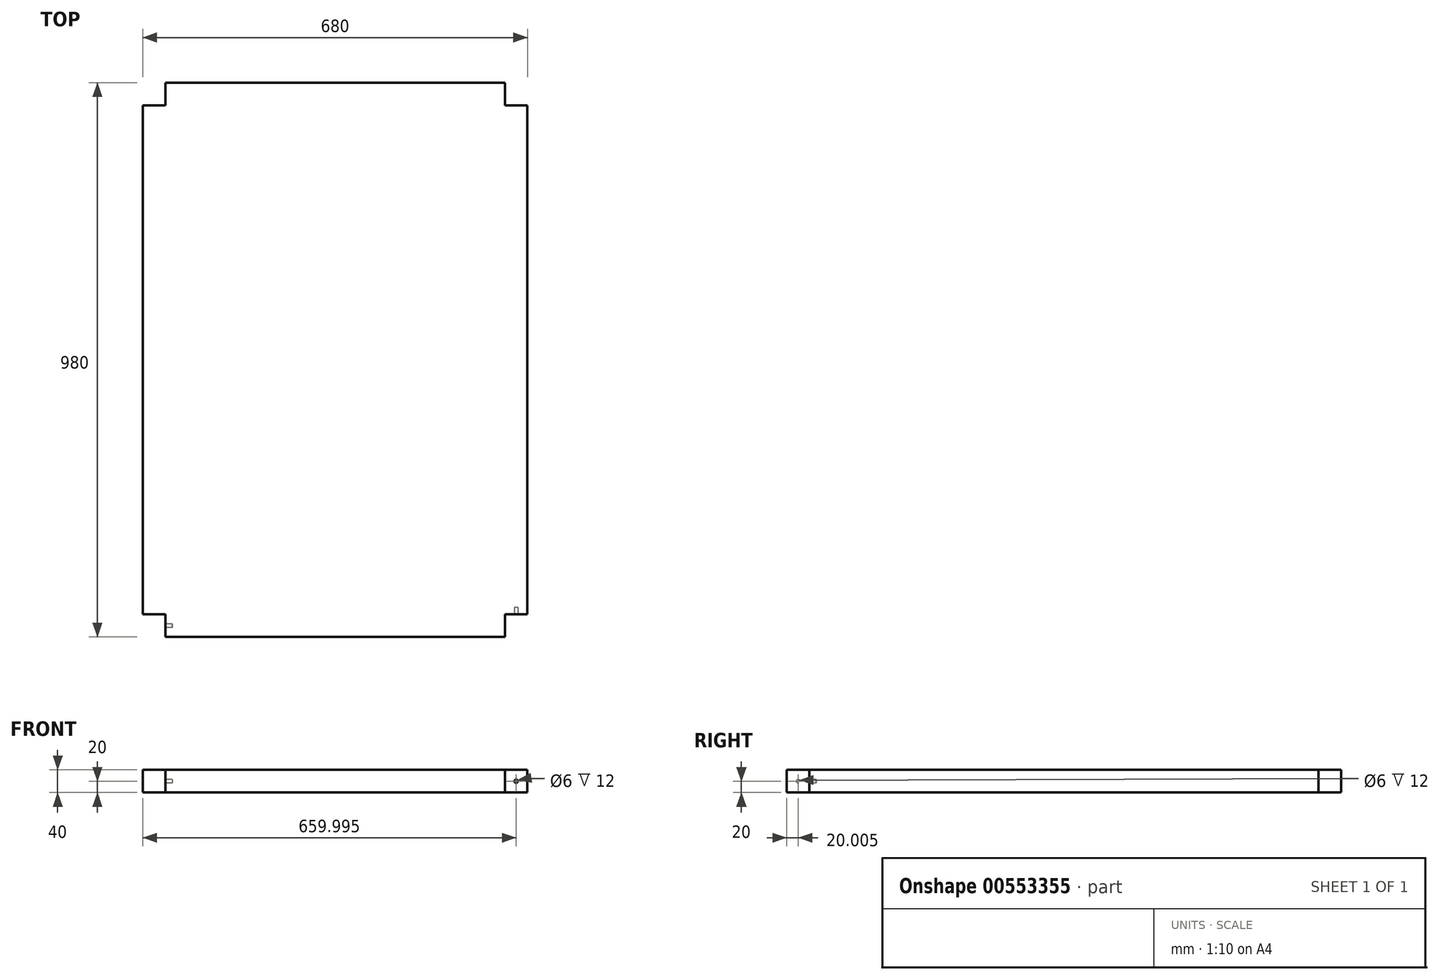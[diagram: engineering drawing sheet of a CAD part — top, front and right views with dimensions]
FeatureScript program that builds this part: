
annotation { "Feature Type Name" : "Feature", "Feature Type Description" : "" }
export const myFeature = defineFeature(function(context is Context, id is Id, definition is map)
    precondition{}
    {
        {
            var Q0;
            Q0=qCreatedBy(makeId("Top.planeOp"),FACE);
            var sketch = newSketch(context, id + "F0", { "sketchPlane" : qUnion([Q0])});
            skLineSegment(sketch, "E0.bottom", {"start": v(-662.47, 921.5) * mm, "end": v(17.53, 921.5) * mm});
            skLineSegment(sketch, "E0.top", {"start": v(-662.47, -58.5) * mm, "end": v(17.53, -58.5) * mm});
            skLineSegment(sketch, "E0.left", {"start": v(-662.47, 921.5) * mm, "end": v(-662.47, -58.5) * mm});
            skLineSegment(sketch, "E0.right", {"start": v(17.53, 921.5) * mm, "end": v(17.53, -58.5) * mm});
            skSolve(sketch);
        }
        {
            var Q0;
            Q0=makeQuery(id+"F0.imprint","IMPRINT",FACE,{"disambiguationData":[TD([[makeQuery(id+"F0.imprint","IMPRINT",EDGE,{"derivedFrom":sQuery(id+"F0.wireOp",EDGE,"E0.bottom")}),-1.0]])]});
            extrude(context, id + "F1", {"entities" : qUnion([Q0]), "depth" : 40 * mm, "offsetDistance" : 25 * mm});
        }
        {
            var Q0;
            Q0=makeQuery(id+"F1.opExtrude","CAP_FACE",FACE,{"disambiguationData":[OSD([sQuery(id+"F0.wireOp",EDGE,"E0.bottom"),sQuery(id+"F0.wireOp",EDGE,"E0.top"),sQuery(id+"F0.wireOp",EDGE,"E0.left"),sQuery(id+"F0.wireOp",EDGE,"E0.right")])],"isStart":false});
            var sketch = newSketch(context, id + "F2", { "sketchPlane" : qUnion([Q0])});
            skLineSegment(sketch, "E1.bottom", {"start": v(-662.47, 921.5) * mm, "end": v(-622.47, 921.5) * mm});
            skLineSegment(sketch, "E1.top", {"start": v(-662.47, 881.5) * mm, "end": v(-622.47, 881.5) * mm});
            skLineSegment(sketch, "E1.left", {"start": v(-662.47, 921.5) * mm, "end": v(-662.47, 881.5) * mm});
            skLineSegment(sketch, "E1.right", {"start": v(-622.47, 921.5) * mm, "end": v(-622.47, 881.5) * mm});
            skLineSegment(sketch, "E2.bottom", {"start": v(17.53, 921.5) * mm, "end": v(-22.47, 921.5) * mm});
            skLineSegment(sketch, "E2.top", {"start": v(17.53, 881.5) * mm, "end": v(-22.47, 881.5) * mm});
            skLineSegment(sketch, "E2.left", {"start": v(17.53, 921.5) * mm, "end": v(17.53, 881.5) * mm});
            skLineSegment(sketch, "E2.right", {"start": v(-22.47, 921.5) * mm, "end": v(-22.47, 881.5) * mm});
            skLineSegment(sketch, "E3.bottom", {"start": v(-662.47, -58.5) * mm, "end": v(-622.47, -58.5) * mm});
            skLineSegment(sketch, "E3.top", {"start": v(-662.47, -18.5) * mm, "end": v(-622.47, -18.5) * mm});
            skLineSegment(sketch, "E3.left", {"start": v(-662.47, -58.5) * mm, "end": v(-662.47, -18.5) * mm});
            skLineSegment(sketch, "E3.right", {"start": v(-622.47, -58.5) * mm, "end": v(-622.47, -18.5) * mm});
            skLineSegment(sketch, "E4.bottom", {"start": v(17.53, -58.5) * mm, "end": v(-22.47, -58.5) * mm});
            skLineSegment(sketch, "E4.top", {"start": v(17.53, -18.5) * mm, "end": v(-22.47, -18.5) * mm});
            skLineSegment(sketch, "E4.left", {"start": v(17.53, -58.5) * mm, "end": v(17.53, -18.5) * mm});
            skLineSegment(sketch, "E4.right", {"start": v(-22.47, -58.5) * mm, "end": v(-22.47, -18.5) * mm});
            skSolve(sketch);
        }
        {
            var Q0;
            Q0=qSketchRegion(id+"F2",true);
            extrude(context, id + "F3", {"entities" : qUnion([Q0]), "operationType" : NewBodyOperationType.REMOVE, "oppositeDirection" : true, "depth" : 40 * mm, "offsetDistance" : 25 * mm});
        }
        {
            var Q0;
            Q0=makeQuery(id+"F3.boolean.opBoolean","COPY",FACE,{"derivedFrom":makeQuery(id+"F3.opExtrude","SWEPT_FACE",FACE,{"disambiguationData":[OSD([sQuery(id+"F2.wireOp",EDGE,"E4.top")])]})});
            var sketch = newSketch(context, id + "F4", { "sketchPlane" : qUnion([Q0])});
            skPoint(sketch, "E5.centerSnap0", {"position": v(-22.47, 20) * mm});
            skCircle(sketch, "E6", {"center": v(-2.47, 20) * mm, "radius": 3 * mm});
            skSolve(sketch);
        }
        {
            var Q0;
            Q0=makeQuery(id+"F4.imprint","IMPRINT",FACE,{"disambiguationData":[TD([[makeQuery(id+"F4.imprint","IMPRINT",EDGE,{"derivedFrom":sQuery(id+"F4.wireOp",EDGE,"E6")}),1.0]])]});
            var Q1;
            Q1=sQuery(id+"F4.wireOp",EDGE,"E6");
            extrude(context, id + "F5", {"entities" : qUnion([Q0]), "operationType" : NewBodyOperationType.REMOVE, "surfaceEntities" : qUnion([Q1]), "oppositeDirection" : true, "depth" : 12 * mm, "offsetDistance" : 25 * mm});
        }
        {
            var Q0;
            Q0=makeQuery(id+"F3.boolean.opBoolean","COPY",FACE,{"derivedFrom":makeQuery(id+"F3.opExtrude","SWEPT_FACE",FACE,{"disambiguationData":[OSD([sQuery(id+"F2.wireOp",EDGE,"E3.right")])]})});
            var sketch = newSketch(context, id + "F6", { "sketchPlane" : qUnion([Q0])});
            skCircle(sketch, "E7", {"center": v(38.5, 20) * mm, "radius": 3 * mm});
            skPoint(sketch, "E7.centerSnap0", {"position": v(38.5, 0) * mm});
            skSolve(sketch);
        }
        {
            var Q0;
            Q0=makeQuery(id+"F6.imprint","IMPRINT",FACE,{"disambiguationData":[TD([[makeQuery(id+"F6.imprint","IMPRINT",EDGE,{"derivedFrom":sQuery(id+"F6.wireOp",EDGE,"E7")}),1.0]])]});
            extrude(context, id + "F7", {"entities" : qUnion([Q0]), "operationType" : NewBodyOperationType.REMOVE, "oppositeDirection" : true, "depth" : 12 * mm, "offsetDistance" : 25 * mm});
        }
    });
